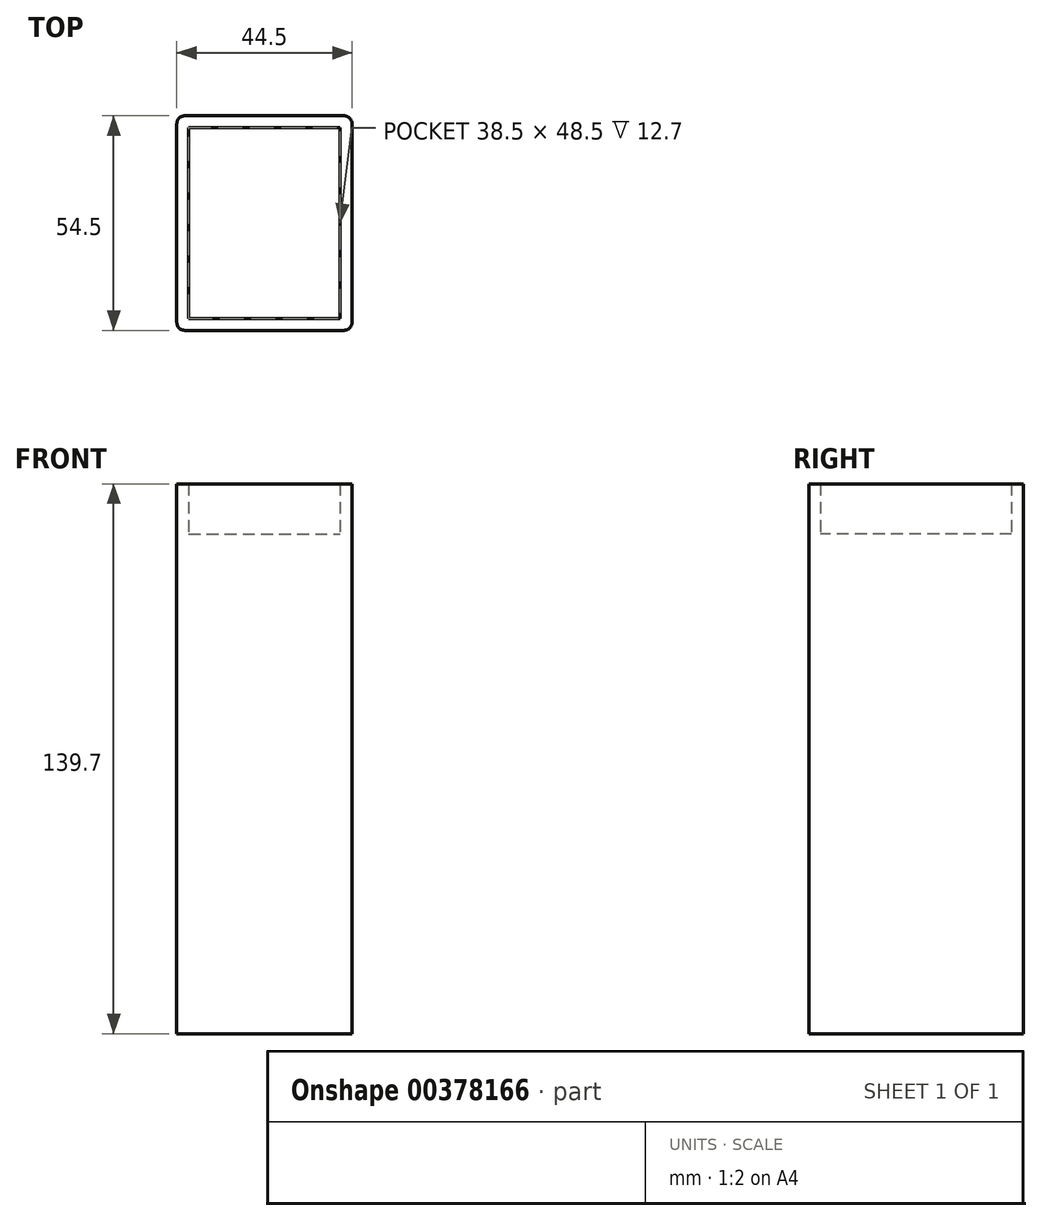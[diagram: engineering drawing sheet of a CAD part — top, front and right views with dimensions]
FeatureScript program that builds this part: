
annotation { "Feature Type Name" : "Feature", "Feature Type Description" : "" }
export const myFeature = defineFeature(function(context is Context, id is Id, definition is map)
    precondition{}
    {
        {
            var Q0;
            Q0=qCreatedBy(makeId("Top.planeOp"),FACE);
            var sketch = newSketch(context, id + "F0", { "sketchPlane" : qUnion([Q0])});
            skLineSegment(sketch, "E0.bottom", {"start": v(-19.25, 24.25) * mm, "end": v(19.25, 24.25) * mm});
            skLineSegment(sketch, "E0.top", {"start": v(-19.25, -24.25) * mm, "end": v(19.25, -24.25) * mm});
            skLineSegment(sketch, "E0.left", {"start": v(-19.25, 24.25) * mm, "end": v(-19.25, -24.25) * mm});
            skLineSegment(sketch, "E0.right", {"start": v(19.25, 24.25) * mm, "end": v(19.25, -24.25) * mm});
            skPoint(sketch, "E0.middle", {"position": v(0, 0) * mm});
            skLineSegment(sketch, "E1.0", {"start": v(-20.25, 27.25) * mm, "end": v(20.25, 27.25) * mm});
            skLineSegment(sketch, "E1.1", {"start": v(-22.25, 25.25) * mm, "end": v(-22.25, -25.25) * mm});
            skLineSegment(sketch, "E1.2", {"start": v(-20.25, -27.25) * mm, "end": v(20.25, -27.25) * mm});
            skLineSegment(sketch, "E1.3", {"start": v(22.25, 25.25) * mm, "end": v(22.25, -25.25) * mm});
            skPoint(sketch, "E2.visualSharp", {"position": v(-22.25, -27.25) * mm});
            skArc(sketch, "E2.filletArc", {"start": v(-22.25, -25.25) * mm, "mid": v(-21.66, -26.66) * mm, "end": v(-20.25, -27.25) * mm});
            skPoint(sketch, "E3.visualSharp", {"position": v(22.25, -27.25) * mm});
            skArc(sketch, "E3.filletArc", {"start": v(20.25, -27.25) * mm, "mid": v(21.66, -26.66) * mm, "end": v(22.25, -25.25) * mm});
            skPoint(sketch, "E4.visualSharp", {"position": v(22.25, 27.25) * mm});
            skArc(sketch, "E4.filletArc", {"start": v(22.25, 25.25) * mm, "mid": v(21.66, 26.66) * mm, "end": v(20.25, 27.25) * mm});
            skPoint(sketch, "E5.visualSharp", {"position": v(-22.25, 27.25) * mm});
            skArc(sketch, "E5.filletArc", {"start": v(-20.25, 27.25) * mm, "mid": v(-21.66, 26.66) * mm, "end": v(-22.25, 25.25) * mm});
            skSolve(sketch);
        }
        {
            var Q0;
            Q0 = qSketchRegion(id + "F0", true);
            extrude(context, id + "F1", {"entities" : qUnion([Q0]), "offsetDistance" : 25 * mm, "depth" : 12.7 * mm});
        }
        {
            var Q0;
            Q0=makeQuery(id+"F0.imprint","IMPRINT",FACE,{"disambiguationData":[TD([[makeQuery(id+"F0.imprint","IMPRINT",EDGE,{"derivedFrom":sQuery(id+"F0.wireOp",EDGE,"E0.bottom")}),-1.0]])]});
            var Q1;
            Q1=makeQuery(id+"F0.imprint","IMPRINT",FACE,{"disambiguationData":[TD([[makeQuery(id+"F0.imprint","IMPRINT",EDGE,{"derivedFrom":sQuery(id+"F0.wireOp",EDGE,"E0.bottom")}),1.0]])]});
            extrude(context, id + "F2", {"entities" : qUnion([Q0, Q1]), "operationType" : NewBodyOperationType.ADD, "oppositeDirection" : true, "offsetDistance" : 25 * mm, "depth" : 127 * mm});
        }
    });
